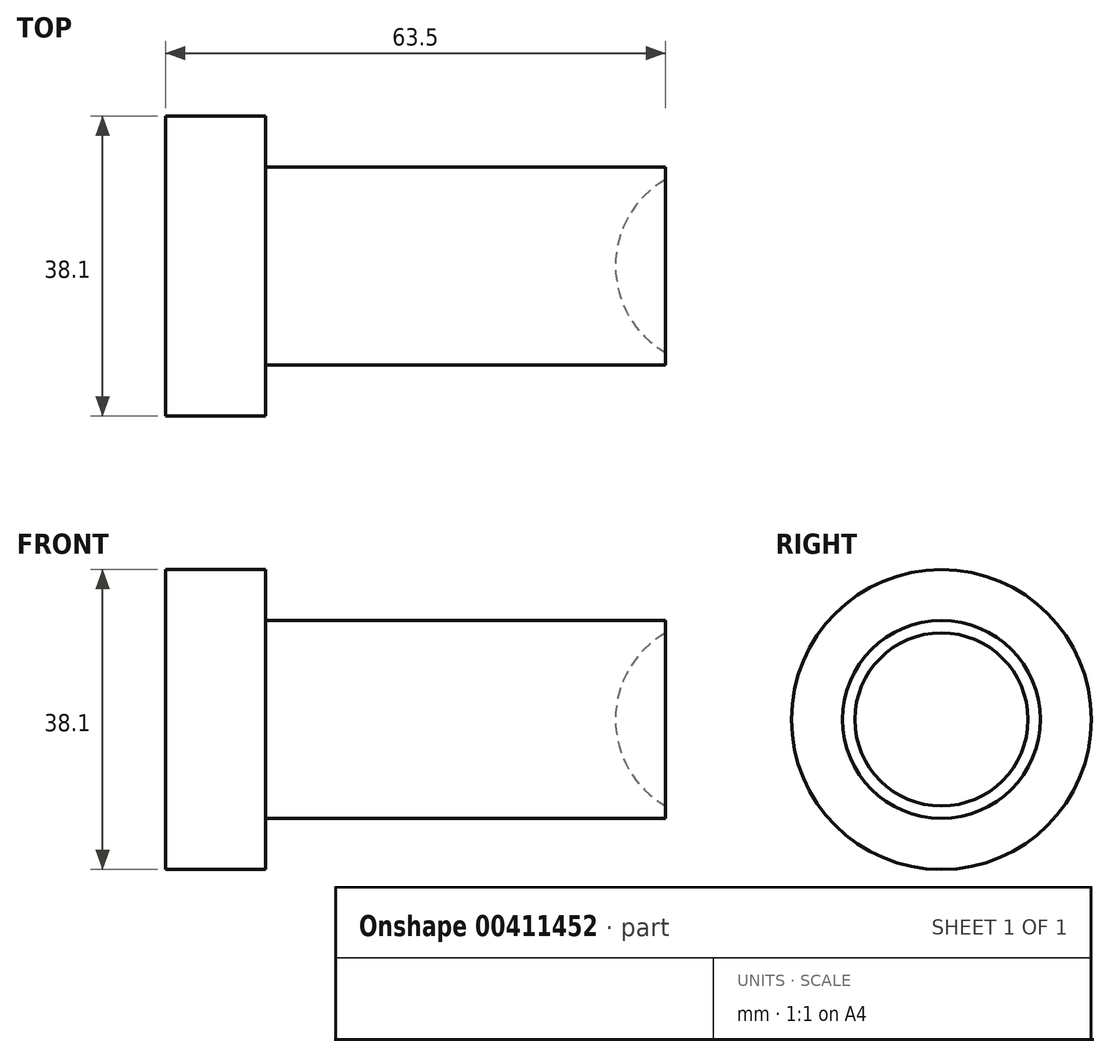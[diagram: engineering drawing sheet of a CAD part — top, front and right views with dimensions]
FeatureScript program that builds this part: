
annotation { "Feature Type Name" : "Feature", "Feature Type Description" : "" }
export const myFeature = defineFeature(function(context is Context, id is Id, definition is map)
    precondition{}
    {
        {
            var Q0;
            Q0=qCreatedBy(makeId("Front.planeOp"),FACE);
            var sketch = newSketch(context, id + "F0", { "sketchPlane" : qUnion([Q0])});
            skLineSegment(sketch, "E0.bottom", {"start": v(-14.1, 0) * mm, "end": v(36.7, 0) * mm});
            skLineSegment(sketch, "E0.top", {"start": v(-14.1, 12.57) * mm, "end": v(36.7, 12.57) * mm});
            skLineSegment(sketch, "E0.left", {"start": v(-14.1, 0) * mm, "end": v(-14.1, 12.57) * mm});
            skLineSegment(sketch, "E0.right", {"start": v(36.7, 0) * mm, "end": v(36.7, 12.57) * mm});
            skLineSegment(sketch, "E1.bottom", {"start": v(-14.1, 0) * mm, "end": v(-26.8, 0) * mm});
            skLineSegment(sketch, "E1.top", {"start": v(-14.1, 19.05) * mm, "end": v(-26.8, 19.05) * mm});
            skLineSegment(sketch, "E1.left", {"start": v(-14.1, 0) * mm, "end": v(-14.1, 19.05) * mm});
            skLineSegment(sketch, "E1.right", {"start": v(-26.8, 0) * mm, "end": v(-26.8, 19.05) * mm});
            skSolve(sketch);
        }
        {
            var Q0;
            {var subQ0=sQuery(id+"F0.wireOp",EDGE,"E0.bottom");Q0=makeQuery(id+"F0.imprint","IMPRINT",FACE,{"disambiguationData":[TD([[makeQuery(id+"F0.imprint","IMPRINT",EDGE,{"derivedFrom":subQ0}),1.0]])]});}
            var Q1;
            {var subQ3=sQuery(id+"F0.wireOp",EDGE,"E1.bottom");Q1=makeQuery(id+"F0.imprint","IMPRINT",FACE,{"disambiguationData":[TD([[makeQuery(id+"F0.imprint","IMPRINT",EDGE,{"derivedFrom":subQ3}),-1.0]])]});}
            var Q2;
            Q2=sQuery(id+"F0.wireOp",EDGE,"E0.bottom");
            revolve(context, id + "F1", {"entities" : qUnion([Q0, Q1]), "axis" : qUnion([Q2]), "revolveType" : RevolveType.FULL});
        }
        {
            var Q0;
            Q0=qCreatedBy(makeId("Front.planeOp"),FACE);
            var sketch = newSketch(context, id + "F2", { "sketchPlane" : qUnion([Q0])});
            skCircle(sketch, "E2", {"center": v(43.06, 0) * mm, "radius": 12.7 * mm});
            skLineSegment(sketch, "E3", {"start": v(43.06, 0) * mm, "end": v(43.06, -12.7) * mm});
            skLineSegment(sketch, "E4", {"start": v(43.06, 0) * mm, "end": v(43.06, 12.7) * mm});
            skSolve(sketch);
        }
        {
            var Q0;
            {var subQ0=sQuery(id+"F2.wireOp",EDGE,"E3");Q0=makeQuery(id+"F2.imprint","IMPRINT",FACE,{"disambiguationData":[TD([[makeQuery(id+"F2.imprint","IMPRINT",EDGE,{"derivedFrom":subQ0}),1.0]])]});}
            var Q1;
            Q1=sQuery(id+"F2.wireOp",EDGE,"E4");
            revolve(context, id + "F3", {"operationType" : NewBodyOperationType.REMOVE, "entities" : qUnion([Q0]), "axis" : qUnion([Q1]), "revolveType" : RevolveType.FULL, "oppositeDirection" : true});
        }
    });
